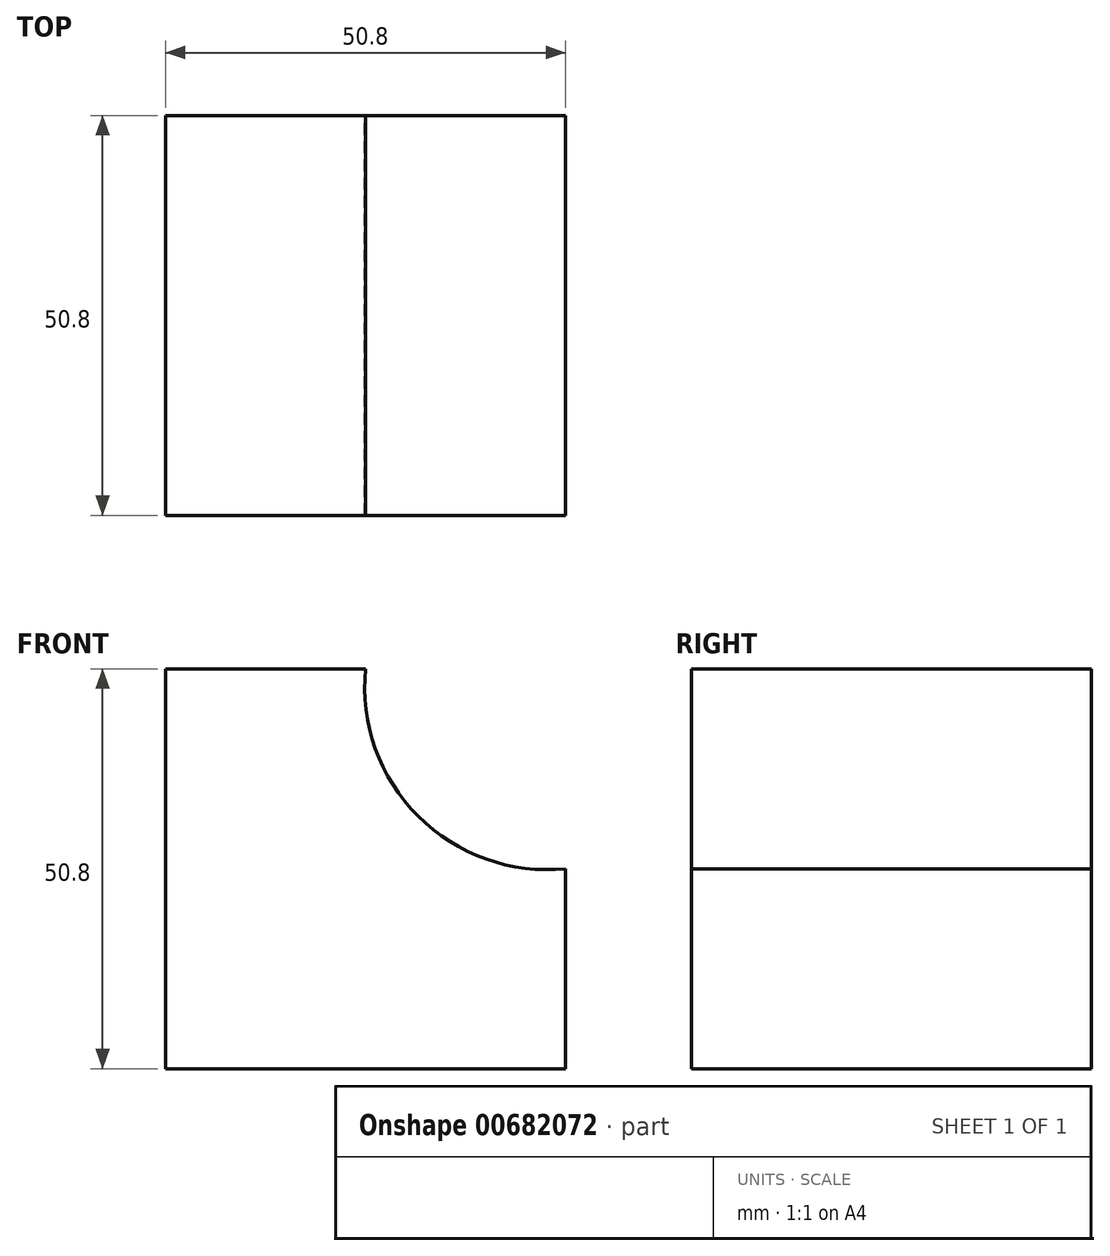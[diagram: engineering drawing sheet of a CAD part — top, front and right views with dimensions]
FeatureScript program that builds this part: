
annotation { "Feature Type Name" : "Feature", "Feature Type Description" : "" }
export const myFeature = defineFeature(function(context is Context, id is Id, definition is map)
    precondition{}
    {
        {
            var Q0;
            Q0=qCreatedBy(makeId("Front.planeOp"),FACE);
            var sketch = newSketch(context, id + "F0", { "sketchPlane" : qUnion([Q0])});
            skLineSegment(sketch, "E0", {"start": v(0, 0) * mm, "end": v(-50.8, 0) * mm});
            skLineSegment(sketch, "E1", {"start": v(-50.8, 0) * mm, "end": v(-50.8, 50.8) * mm});
            skLineSegment(sketch, "E2", {"start": v(-50.8, 50.8) * mm, "end": v(-25.4, 50.8) * mm});
            skLineSegment(sketch, "E3", {"start": v(0, 0) * mm, "end": v(0, 25.4) * mm});
            skArc(sketch, "E4", {"start": v(-25.4, 50.8) * mm, "mid": v(-18.72, 32.08) * mm, "end": v(0, 25.4) * mm});
            skSolve(sketch);
        }
        {
            var Q0;
            Q0 = qSketchRegion(id + "F0", true);
            extrude(context, id + "F1", {"entities" : qUnion([Q0]), "depth" : 50.8 * mm, "offsetDistance" : 25.4 * mm});
        }
    });
